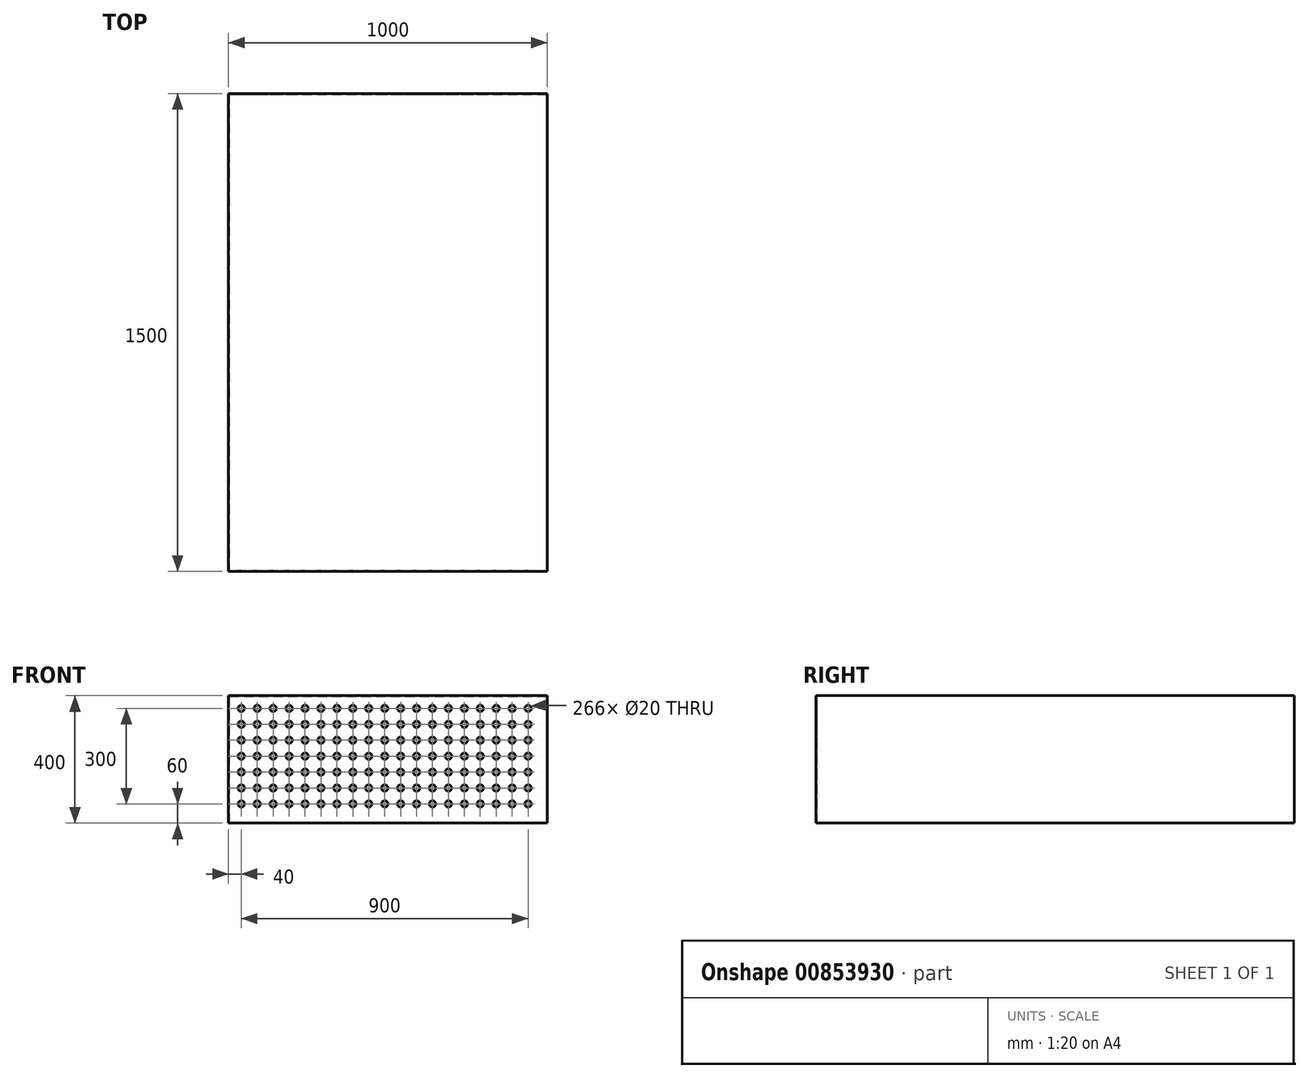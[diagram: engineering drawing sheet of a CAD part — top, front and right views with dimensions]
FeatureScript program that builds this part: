
annotation { "Feature Type Name" : "Feature", "Feature Type Description" : "" }
export const myFeature = defineFeature(function(context is Context, id is Id, definition is map)
    precondition{}
    {
        {
            var Q0;
            Q0=qCreatedBy(makeId("Top.planeOp"),FACE);
            var sketch = newSketch(context, id + "F0", { "sketchPlane" : qUnion([Q0])});
            skLineSegment(sketch, "E0.bottom", {"start": v(0, 0) * mm, "end": v(1000, 0) * mm});
            skLineSegment(sketch, "E0.top", {"start": v(0, -1500) * mm, "end": v(1000, -1500) * mm});
            skLineSegment(sketch, "E0.left", {"start": v(0, 0) * mm, "end": v(0, -1500) * mm});
            skLineSegment(sketch, "E0.right", {"start": v(1000, 0) * mm, "end": v(1000, -1500) * mm});
            skSolve(sketch);
        }
        {
            var Q0;
            Q0=makeQuery(id+"F0.imprint","IMPRINT",FACE,{"disambiguationData":[TD([[makeQuery(id+"F0.imprint","IMPRINT",EDGE,{"derivedFrom":sQuery(id+"F0.wireOp",EDGE,"E0.bottom")}),-1.0]])]});
            extrude(context, id + "F1", {"entities" : qUnion([Q0]), "depth" : 400 * mm, "offsetDistance" : 25 * mm});
        }
        {
            var Q0;
            Q0=makeQuery(id+"F1.opExtrude","CAP_FACE",FACE,{"disambiguationData":[OSD([sQuery(id+"F0.wireOp",EDGE,"E0.bottom"),sQuery(id+"F0.wireOp",EDGE,"E0.top"),sQuery(id+"F0.wireOp",EDGE,"E0.left"),sQuery(id+"F0.wireOp",EDGE,"E0.right")])],"isStart":true});
            shell(context, id + "F2", {"entities" : qUnion([Q0]), "thickness" : 2.5 * mm});
        }
        {
            var Q0;
            Q0=makeQuery(id+"F1.opExtrude","SWEPT_FACE",FACE,{"disambiguationData":[OSD([sQuery(id+"F0.wireOp",EDGE,"E0.top")])]});
            var sketch = newSketch(context, id + "F3", { "sketchPlane" : qUnion([Q0])});
            skCircle(sketch, "E1", {"center": v(40, 360) * mm, "radius": 10 * mm});
            skCircle(sketch, "E2.0.1.0", {"center": v(40, 310) * mm, "radius": 10 * mm});
            skCircle(sketch, "E2.0.2.0", {"center": v(40, 260) * mm, "radius": 10 * mm});
            skCircle(sketch, "E2.0.3.0", {"center": v(40, 210) * mm, "radius": 10 * mm});
            skCircle(sketch, "E2.0.4.0", {"center": v(40, 160) * mm, "radius": 10 * mm});
            skCircle(sketch, "E2.0.5.0", {"center": v(40, 110) * mm, "radius": 10 * mm});
            skCircle(sketch, "E2.0.6.0", {"center": v(40, 60) * mm, "radius": 10 * mm});
            skCircle(sketch, "E2.1.0.0", {"center": v(90, 360) * mm, "radius": 10 * mm});
            skCircle(sketch, "E2.1.1.0", {"center": v(90, 310) * mm, "radius": 10 * mm});
            skCircle(sketch, "E2.1.2.0", {"center": v(90, 260) * mm, "radius": 10 * mm});
            skCircle(sketch, "E2.1.3.0", {"center": v(90, 210) * mm, "radius": 10 * mm});
            skCircle(sketch, "E2.1.4.0", {"center": v(90, 160) * mm, "radius": 10 * mm});
            skCircle(sketch, "E2.1.5.0", {"center": v(90, 110) * mm, "radius": 10 * mm});
            skCircle(sketch, "E2.1.6.0", {"center": v(90, 60) * mm, "radius": 10 * mm});
            skCircle(sketch, "E2.2.0.0", {"center": v(140, 360) * mm, "radius": 10 * mm});
            skCircle(sketch, "E2.2.1.0", {"center": v(140, 310) * mm, "radius": 10 * mm});
            skCircle(sketch, "E2.2.2.0", {"center": v(140, 260) * mm, "radius": 10 * mm});
            skCircle(sketch, "E2.2.3.0", {"center": v(140, 210) * mm, "radius": 10 * mm});
            skCircle(sketch, "E2.2.4.0", {"center": v(140, 160) * mm, "radius": 10 * mm});
            skCircle(sketch, "E2.2.5.0", {"center": v(140, 110) * mm, "radius": 10 * mm});
            skCircle(sketch, "E2.2.6.0", {"center": v(140, 60) * mm, "radius": 10 * mm});
            skCircle(sketch, "E2.3.0.0", {"center": v(190, 360) * mm, "radius": 10 * mm});
            skCircle(sketch, "E2.3.1.0", {"center": v(190, 310) * mm, "radius": 10 * mm});
            skCircle(sketch, "E2.3.2.0", {"center": v(190, 260) * mm, "radius": 10 * mm});
            skCircle(sketch, "E2.3.3.0", {"center": v(190, 210) * mm, "radius": 10 * mm});
            skCircle(sketch, "E2.3.4.0", {"center": v(190, 160) * mm, "radius": 10 * mm});
            skCircle(sketch, "E2.3.5.0", {"center": v(190, 110) * mm, "radius": 10 * mm});
            skCircle(sketch, "E2.3.6.0", {"center": v(190, 60) * mm, "radius": 10 * mm});
            skCircle(sketch, "E2.4.0.0", {"center": v(240, 360) * mm, "radius": 10 * mm});
            skCircle(sketch, "E2.4.1.0", {"center": v(240, 310) * mm, "radius": 10 * mm});
            skCircle(sketch, "E2.4.2.0", {"center": v(240, 260) * mm, "radius": 10 * mm});
            skCircle(sketch, "E2.4.3.0", {"center": v(240, 210) * mm, "radius": 10 * mm});
            skCircle(sketch, "E2.4.4.0", {"center": v(240, 160) * mm, "radius": 10 * mm});
            skCircle(sketch, "E2.4.5.0", {"center": v(240, 110) * mm, "radius": 10 * mm});
            skCircle(sketch, "E2.4.6.0", {"center": v(240, 60) * mm, "radius": 10 * mm});
            skCircle(sketch, "E2.5.0.0", {"center": v(290, 360) * mm, "radius": 10 * mm});
            skCircle(sketch, "E2.5.1.0", {"center": v(290, 310) * mm, "radius": 10 * mm});
            skCircle(sketch, "E2.5.2.0", {"center": v(290, 260) * mm, "radius": 10 * mm});
            skCircle(sketch, "E2.5.3.0", {"center": v(290, 210) * mm, "radius": 10 * mm});
            skCircle(sketch, "E2.5.4.0", {"center": v(290, 160) * mm, "radius": 10 * mm});
            skCircle(sketch, "E2.5.5.0", {"center": v(290, 110) * mm, "radius": 10 * mm});
            skCircle(sketch, "E2.5.6.0", {"center": v(290, 60) * mm, "radius": 10 * mm});
            skCircle(sketch, "E2.6.0.0", {"center": v(340, 360) * mm, "radius": 10 * mm});
            skCircle(sketch, "E2.6.1.0", {"center": v(340, 310) * mm, "radius": 10 * mm});
            skCircle(sketch, "E2.6.2.0", {"center": v(340, 260) * mm, "radius": 10 * mm});
            skCircle(sketch, "E2.6.3.0", {"center": v(340, 210) * mm, "radius": 10 * mm});
            skCircle(sketch, "E2.6.4.0", {"center": v(340, 160) * mm, "radius": 10 * mm});
            skCircle(sketch, "E2.6.5.0", {"center": v(340, 110) * mm, "radius": 10 * mm});
            skCircle(sketch, "E2.6.6.0", {"center": v(340, 60) * mm, "radius": 10 * mm});
            skCircle(sketch, "E2.7.0.0", {"center": v(390, 360) * mm, "radius": 10 * mm});
            skCircle(sketch, "E2.7.1.0", {"center": v(390, 310) * mm, "radius": 10 * mm});
            skCircle(sketch, "E2.7.2.0", {"center": v(390, 260) * mm, "radius": 10 * mm});
            skCircle(sketch, "E2.7.3.0", {"center": v(390, 210) * mm, "radius": 10 * mm});
            skCircle(sketch, "E2.7.4.0", {"center": v(390, 160) * mm, "radius": 10 * mm});
            skCircle(sketch, "E2.7.5.0", {"center": v(390, 110) * mm, "radius": 10 * mm});
            skCircle(sketch, "E2.7.6.0", {"center": v(390, 60) * mm, "radius": 10 * mm});
            skCircle(sketch, "E2.8.0.0", {"center": v(440, 360) * mm, "radius": 10 * mm});
            skCircle(sketch, "E2.8.1.0", {"center": v(440, 310) * mm, "radius": 10 * mm});
            skCircle(sketch, "E2.8.2.0", {"center": v(440, 260) * mm, "radius": 10 * mm});
            skCircle(sketch, "E2.8.3.0", {"center": v(440, 210) * mm, "radius": 10 * mm});
            skCircle(sketch, "E2.8.4.0", {"center": v(440, 160) * mm, "radius": 10 * mm});
            skCircle(sketch, "E2.8.5.0", {"center": v(440, 110) * mm, "radius": 10 * mm});
            skCircle(sketch, "E2.8.6.0", {"center": v(440, 60) * mm, "radius": 10 * mm});
            skLineSegment(sketch, "E2.direction1", {"start": v(40, 360) * mm, "end": v(90, 360) * mm, "construction": true});
            skLineSegment(sketch, "E2.direction2", {"start": v(40, 360) * mm, "end": v(40, 310) * mm, "construction": true});
            skCircle(sketch, "E3.0.9.0", {"center": v(490, 360) * mm, "radius": 10 * mm});
            skCircle(sketch, "E3.0.9.1", {"center": v(490, 310) * mm, "radius": 10 * mm});
            skCircle(sketch, "E3.0.9.2", {"center": v(490, 260) * mm, "radius": 10 * mm});
            skCircle(sketch, "E3.0.9.3", {"center": v(490, 210) * mm, "radius": 10 * mm});
            skCircle(sketch, "E3.0.9.4", {"center": v(490, 160) * mm, "radius": 10 * mm});
            skCircle(sketch, "E3.0.9.5", {"center": v(490, 110) * mm, "radius": 10 * mm});
            skCircle(sketch, "E3.0.9.6", {"center": v(490, 60) * mm, "radius": 10 * mm});
            skCircle(sketch, "E3.0.10.0", {"center": v(540, 360) * mm, "radius": 10 * mm});
            skCircle(sketch, "E3.0.10.1", {"center": v(540, 310) * mm, "radius": 10 * mm});
            skCircle(sketch, "E3.0.10.2", {"center": v(540, 260) * mm, "radius": 10 * mm});
            skCircle(sketch, "E3.0.10.3", {"center": v(540, 210) * mm, "radius": 10 * mm});
            skCircle(sketch, "E3.0.10.4", {"center": v(540, 160) * mm, "radius": 10 * mm});
            skCircle(sketch, "E3.0.10.5", {"center": v(540, 110) * mm, "radius": 10 * mm});
            skCircle(sketch, "E3.0.10.6", {"center": v(540, 60) * mm, "radius": 10 * mm});
            skCircle(sketch, "E3.0.11.0", {"center": v(590, 360) * mm, "radius": 10 * mm});
            skCircle(sketch, "E3.0.11.1", {"center": v(590, 310) * mm, "radius": 10 * mm});
            skCircle(sketch, "E3.0.11.2", {"center": v(590, 260) * mm, "radius": 10 * mm});
            skCircle(sketch, "E3.0.11.3", {"center": v(590, 210) * mm, "radius": 10 * mm});
            skCircle(sketch, "E3.0.11.4", {"center": v(590, 160) * mm, "radius": 10 * mm});
            skCircle(sketch, "E3.0.11.5", {"center": v(590, 110) * mm, "radius": 10 * mm});
            skCircle(sketch, "E3.0.11.6", {"center": v(590, 60) * mm, "radius": 10 * mm});
            skCircle(sketch, "E3.0.12.0", {"center": v(640, 360) * mm, "radius": 10 * mm});
            skCircle(sketch, "E3.0.12.1", {"center": v(640, 310) * mm, "radius": 10 * mm});
            skCircle(sketch, "E3.0.12.2", {"center": v(640, 260) * mm, "radius": 10 * mm});
            skCircle(sketch, "E3.0.12.3", {"center": v(640, 210) * mm, "radius": 10 * mm});
            skCircle(sketch, "E3.0.12.4", {"center": v(640, 160) * mm, "radius": 10 * mm});
            skCircle(sketch, "E3.0.12.5", {"center": v(640, 110) * mm, "radius": 10 * mm});
            skCircle(sketch, "E3.0.12.6", {"center": v(640, 60) * mm, "radius": 10 * mm});
            skCircle(sketch, "E3.0.13.0", {"center": v(690, 360) * mm, "radius": 10 * mm});
            skCircle(sketch, "E3.0.13.1", {"center": v(690, 310) * mm, "radius": 10 * mm});
            skCircle(sketch, "E3.0.13.2", {"center": v(690, 260) * mm, "radius": 10 * mm});
            skCircle(sketch, "E3.0.13.3", {"center": v(690, 210) * mm, "radius": 10 * mm});
            skCircle(sketch, "E3.0.13.4", {"center": v(690, 160) * mm, "radius": 10 * mm});
            skCircle(sketch, "E3.0.13.5", {"center": v(690, 110) * mm, "radius": 10 * mm});
            skCircle(sketch, "E3.0.13.6", {"center": v(690, 60) * mm, "radius": 10 * mm});
            skCircle(sketch, "E3.0.14.0", {"center": v(740, 360) * mm, "radius": 10 * mm});
            skCircle(sketch, "E3.0.14.1", {"center": v(740, 310) * mm, "radius": 10 * mm});
            skCircle(sketch, "E3.0.14.2", {"center": v(740, 260) * mm, "radius": 10 * mm});
            skCircle(sketch, "E3.0.14.3", {"center": v(740, 210) * mm, "radius": 10 * mm});
            skCircle(sketch, "E3.0.14.4", {"center": v(740, 160) * mm, "radius": 10 * mm});
            skCircle(sketch, "E3.0.14.5", {"center": v(740, 110) * mm, "radius": 10 * mm});
            skCircle(sketch, "E3.0.14.6", {"center": v(740, 60) * mm, "radius": 10 * mm});
            skCircle(sketch, "E3.0.15.0", {"center": v(790, 360) * mm, "radius": 10 * mm});
            skCircle(sketch, "E3.0.15.1", {"center": v(790, 310) * mm, "radius": 10 * mm});
            skCircle(sketch, "E3.0.15.2", {"center": v(790, 260) * mm, "radius": 10 * mm});
            skCircle(sketch, "E3.0.15.3", {"center": v(790, 210) * mm, "radius": 10 * mm});
            skCircle(sketch, "E3.0.15.4", {"center": v(790, 160) * mm, "radius": 10 * mm});
            skCircle(sketch, "E3.0.15.5", {"center": v(790, 110) * mm, "radius": 10 * mm});
            skCircle(sketch, "E3.0.15.6", {"center": v(790, 60) * mm, "radius": 10 * mm});
            skCircle(sketch, "E3.0.16.0", {"center": v(840, 360) * mm, "radius": 10 * mm});
            skCircle(sketch, "E3.0.16.1", {"center": v(840, 310) * mm, "radius": 10 * mm});
            skCircle(sketch, "E3.0.16.2", {"center": v(840, 260) * mm, "radius": 10 * mm});
            skCircle(sketch, "E3.0.16.3", {"center": v(840, 210) * mm, "radius": 10 * mm});
            skCircle(sketch, "E3.0.16.4", {"center": v(840, 160) * mm, "radius": 10 * mm});
            skCircle(sketch, "E3.0.16.5", {"center": v(840, 110) * mm, "radius": 10 * mm});
            skCircle(sketch, "E3.0.16.6", {"center": v(840, 60) * mm, "radius": 10 * mm});
            skCircle(sketch, "E3.0.17.0", {"center": v(890, 360) * mm, "radius": 10 * mm});
            skCircle(sketch, "E3.0.17.1", {"center": v(890, 310) * mm, "radius": 10 * mm});
            skCircle(sketch, "E3.0.17.2", {"center": v(890, 260) * mm, "radius": 10 * mm});
            skCircle(sketch, "E3.0.17.3", {"center": v(890, 210) * mm, "radius": 10 * mm});
            skCircle(sketch, "E3.0.17.4", {"center": v(890, 160) * mm, "radius": 10 * mm});
            skCircle(sketch, "E3.0.17.5", {"center": v(890, 110) * mm, "radius": 10 * mm});
            skCircle(sketch, "E3.0.17.6", {"center": v(890, 60) * mm, "radius": 10 * mm});
            skCircle(sketch, "E3.0.18.0", {"center": v(940, 360) * mm, "radius": 10 * mm});
            skCircle(sketch, "E3.0.18.1", {"center": v(940, 310) * mm, "radius": 10 * mm});
            skCircle(sketch, "E3.0.18.2", {"center": v(940, 260) * mm, "radius": 10 * mm});
            skCircle(sketch, "E3.0.18.3", {"center": v(940, 210) * mm, "radius": 10 * mm});
            skCircle(sketch, "E3.0.18.4", {"center": v(940, 160) * mm, "radius": 10 * mm});
            skCircle(sketch, "E3.0.18.5", {"center": v(940, 110) * mm, "radius": 10 * mm});
            skCircle(sketch, "E3.0.18.6", {"center": v(940, 60) * mm, "radius": 10 * mm});
            skSolve(sketch);
        }
        {
            var Q0;
            Q0 = qSketchRegion(id + "F3", true);
            extrude(context, id + "F4", {"entities" : qUnion([Q0]), "operationType" : NewBodyOperationType.REMOVE, "oppositeDirection" : true, "depth" : 2000 * mm, "offsetDistance" : 25 * mm});
        }
    });
